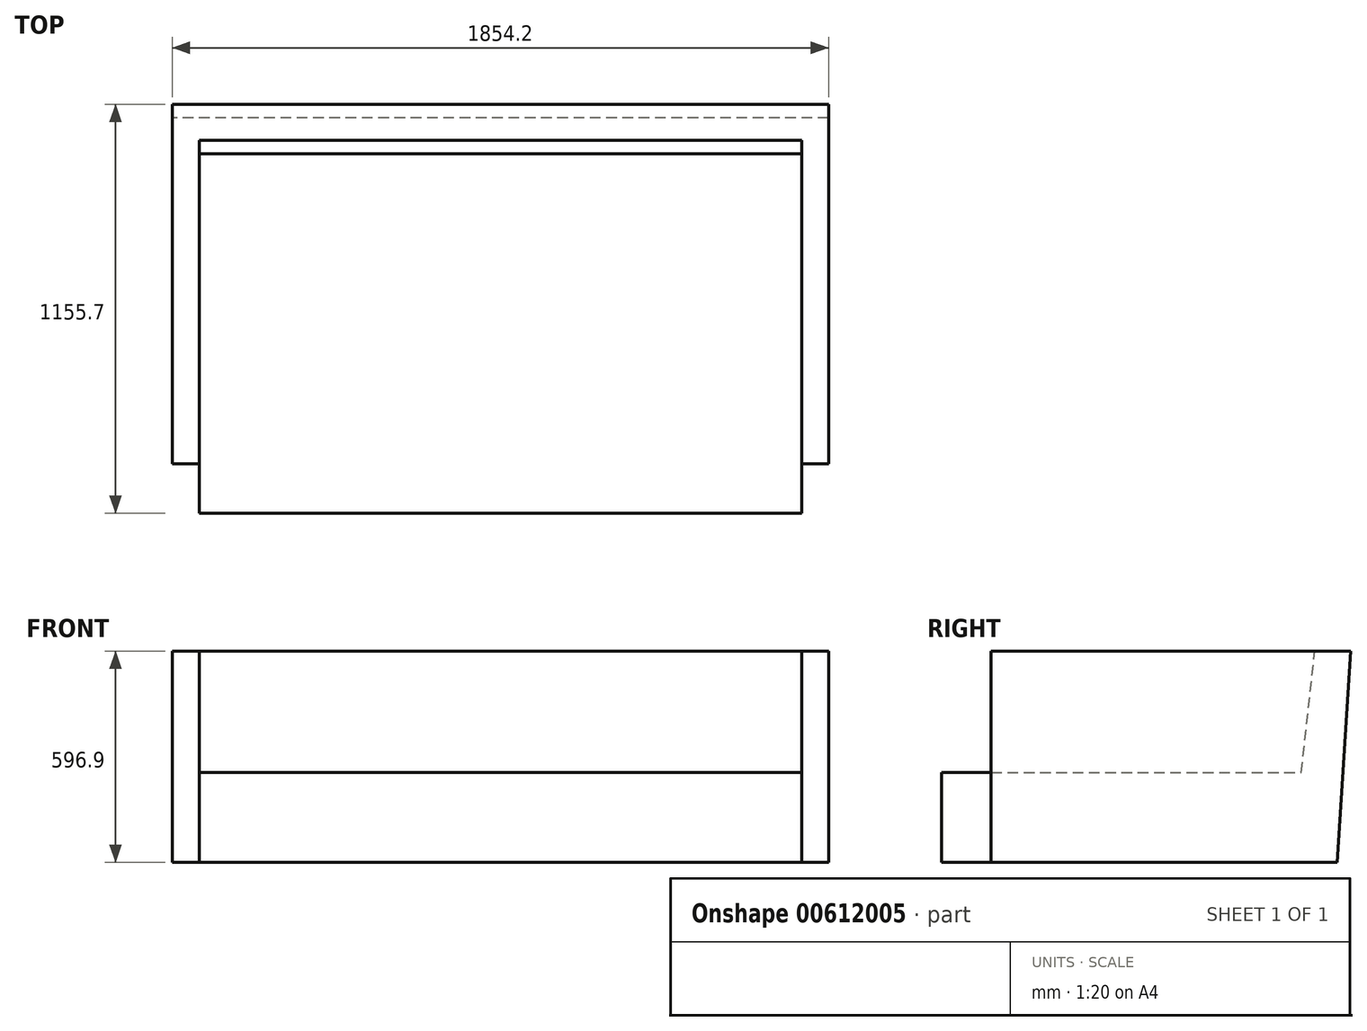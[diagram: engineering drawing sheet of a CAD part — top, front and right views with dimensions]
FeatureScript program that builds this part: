
annotation { "Feature Type Name" : "Feature", "Feature Type Description" : "" }
export const myFeature = defineFeature(function(context is Context, id is Id, definition is map)
    precondition{}
    {
        {
            var Q0;
            Q0=qCreatedBy(makeId("Right.planeOp"),FACE);
            var sketch = newSketch(context, id + "F0", { "sketchPlane" : qUnion([Q0])});
            skLineSegment(sketch, "E0", {"start": v(-658.55, 0) * mm, "end": v(-658.55, 596.9) * mm});
            skLineSegment(sketch, "E1", {"start": v(-658.55, 596.9) * mm, "end": v(357.45, 596.9) * mm});
            skLineSegment(sketch, "E2", {"start": v(357.45, 596.9) * mm, "end": v(319.35, 0) * mm});
            skLineSegment(sketch, "E3", {"start": v(319.35, 0) * mm, "end": v(-658.55, 0) * mm});
            skSolve(sketch);
        }
        {
            var Q0;
            Q0 = qSketchRegion(id + "F0", true);
            extrude(context, id + "F1", {"entities" : qUnion([Q0]), "endBound" : BoundingType.SYMMETRIC, "depth" : 1854.2 * mm, "offsetDistance" : 25.4 * mm});
        }
        {
            var Q0;
            Q0=qCreatedBy(makeId("Right.planeOp"),FACE);
            var sketch = newSketch(context, id + "F2", { "sketchPlane" : qUnion([Q0])});
            skLineSegment(sketch, "E4", {"start": v(-658.55, 254) * mm, "end": v(217.75, 254) * mm});
            skLineSegment(sketch, "E5", {"start": v(217.75, 254) * mm, "end": v(255.85, 596.9) * mm});
            skLineSegment(sketch, "E6", {"start": v(255.85, 596.9) * mm, "end": v(-658.55, 596.9) * mm});
            skLineSegment(sketch, "E7", {"start": v(-658.55, 596.9) * mm, "end": v(-658.55, 254) * mm});
            skSolve(sketch);
        }
        {
            var Q0;
            Q0 = qSketchRegion(id + "F2", true);
            extrude(context, id + "F3", {"entities" : qUnion([Q0]), "operationType" : NewBodyOperationType.REMOVE, "endBound" : BoundingType.SYMMETRIC, "oppositeDirection" : true, "depth" : 1701.8 * mm, "offsetDistance" : 25.4 * mm});
        }
        {
            var Q0;
            Q0=qCreatedBy(makeId("Right.planeOp"),FACE);
            var sketch = newSketch(context, id + "F4", { "sketchPlane" : qUnion([Q0])});
            skLineSegment(sketch, "E8.bottom", {"start": v(-658.55, 0) * mm, "end": v(-798.25, 0) * mm});
            skLineSegment(sketch, "E8.top", {"start": v(-658.55, 254) * mm, "end": v(-798.25, 254) * mm});
            skLineSegment(sketch, "E8.left", {"start": v(-658.55, 0) * mm, "end": v(-658.55, 254) * mm});
            skLineSegment(sketch, "E8.right", {"start": v(-798.25, 0) * mm, "end": v(-798.25, 254) * mm});
            skSolve(sketch);
        }
        {
            var Q0;
            Q0 = qSketchRegion(id + "F4", true);
            extrude(context, id + "F5", {"entities" : qUnion([Q0]), "operationType" : NewBodyOperationType.ADD, "endBound" : BoundingType.SYMMETRIC, "depth" : 1701.8 * mm, "offsetDistance" : 25.4 * mm});
        }
    });
